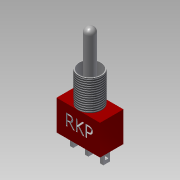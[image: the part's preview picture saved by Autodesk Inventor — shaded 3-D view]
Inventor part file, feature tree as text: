
AUTODESK INVENTOR PART (.ipt)
format: ipt  version: 2015 SP1 (Build 190203100, 203)  size: 329,728 bytes
history: native  units: mm
features: extrude x6, sketch x6, thread x1, shell x1, fillet x1, projected_geometry x1
ambient origin geometry x8: Origin, YZ Plane, XZ Plane, XY Plane, X Axis, Y Axis, Z Axis, Center Point
bodies: Solid1 (feature_tree)
feature tree (16):
  extrude  "Extrusion1"  Depth=7.0mm
  extrude  "Extrusion2"  Depth=7.0mm
  thread  "Thread1"  [1 undecoded]
  extrude  "Extrusion3"  Depth=1.0mm
  extrude  "Extrusion4"  Depth=20.0mm
  shell  "Shell1"  Thickness=4.0mm
  extrude  "Extrusion5"  Depth=2.0mm
  fillet  "Fillet1"  Radius=0.25mm
  extrude  "Extrusion6"  Depth=1.5mm
  sketch  "Sketch1"  dims[d0=13.0mm d1=7.0mm]
  sketch  "Sketch2"  dims[d2=9.0mm d3=0.0mm d4=7.0mm d5=9.0mm d6=0.0mm]
  sketch  "Sketch3"  dims[d7=10.0mm d8=0.0mm d9=1.0mm]
  sketch  "Sketch4"  dims[d10=2.0mm d11=20.0mm d13=4.5mm d14=20.0mm d16=4.5mm d19=4.0mm d20=0.0mm]
  projected_geometry  "Projected Loop1"
  sketch  "Sketch5"  dims[d21=1.0mm d22=2.0mm d23=0.25mm]
  sketch  "Sketch6"  dims[d24=4.0mm d25=0.0mm d26=0.3mm d27=3.0mm d28=20.0mm d29=0.0mm d30=1.5mm d31=10.0mm d32=0.0mm]
note: 1 required parameter value undecoded (feature->parameter linkage not recoverable at this tier; creation-order binding heuristic only, values carry confidence <= 0.55)
